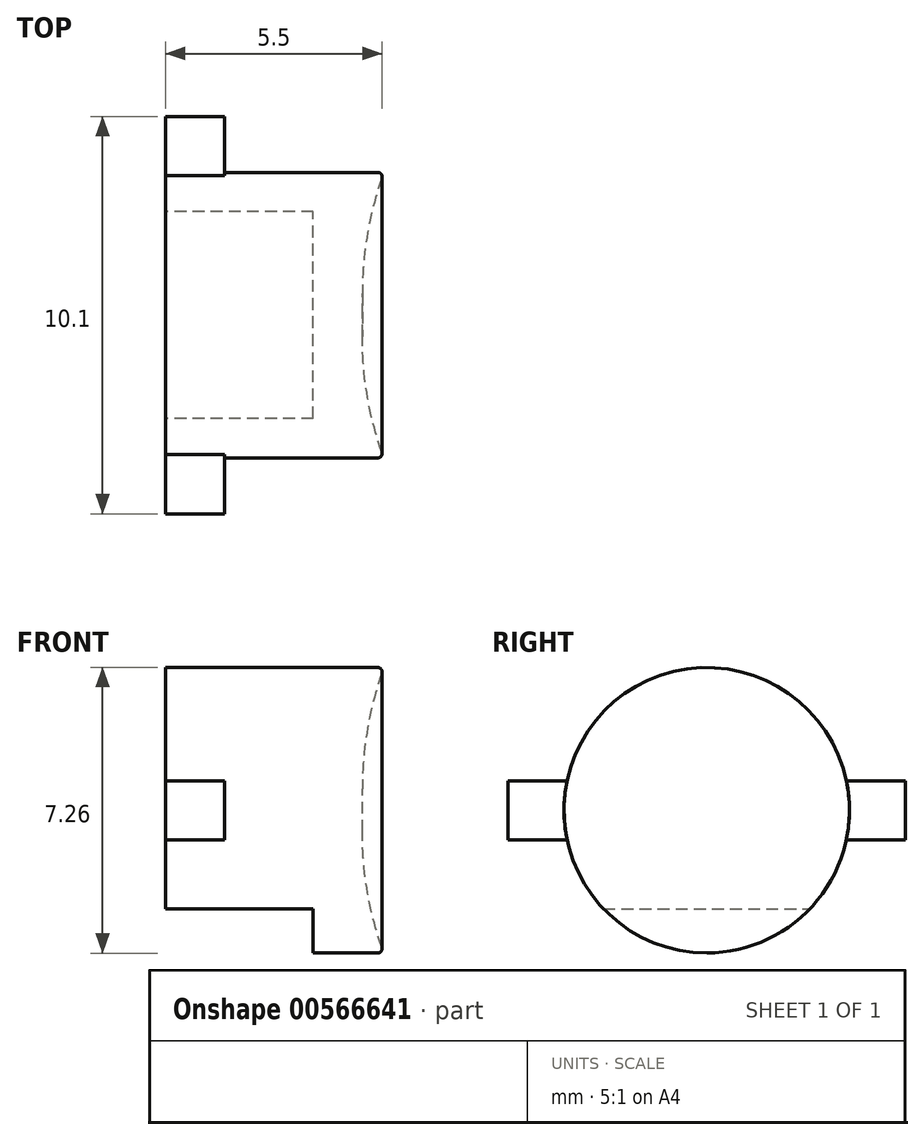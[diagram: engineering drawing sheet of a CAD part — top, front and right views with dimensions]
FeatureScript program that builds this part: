
annotation { "Feature Type Name" : "Feature", "Feature Type Description" : "" }
export const myFeature = defineFeature(function(context is Context, id is Id, definition is map)
    precondition{}
    {
        {
            var Q0;
            Q0=qCreatedBy(makeId("Right.planeOp"),FACE);
            var sketch = newSketch(context, id + "F0", { "sketchPlane" : qUnion([Q0])});
            skCircle(sketch, "E0", {"center": v(0, 0) * mm, "radius": 3.62 * mm});
            skSolve(sketch);
        }
        {
            var Q0;
            Q0=makeQuery(id+"F0.imprint","IMPRINT",FACE,{"disambiguationData":[TD([[makeQuery(id+"F0.imprint","IMPRINT",EDGE,{"derivedFrom":sQuery(id+"F0.wireOp",EDGE,"E0")}),1.0]])]});
            extrude(context, id + "F1", {"entities" : qUnion([Q0]), "endBound" : BoundingType.SYMMETRIC, "depth" : 5.5 * mm, "offsetDistance" : 25 * mm});
        }
        {
            var Q0;
            Q0=makeQuery(id+"F1.opExtrude","CAP_FACE",FACE,{"disambiguationData":[OSD([sQuery(id+"F0.wireOp",EDGE,"E0")])],"isStart":true});
            var sketch = newSketch(context, id + "F2", { "sketchPlane" : qUnion([Q0])});
            skLineSegment(sketch, "E1.left", {"start": v(5.05, -0.75) * mm, "end": v(5.05, 0.75) * mm});
            skLineSegment(sketch, "E2.left", {"start": v(-5.05, 0.75) * mm, "end": v(-5.05, -0.75) * mm});
            skLineSegment(sketch, "E3", {"start": v(5.05, 0.75) * mm, "end": v(3.55, 0.75) * mm});
            skLineSegment(sketch, "E4", {"start": v(5.05, -0.75) * mm, "end": v(3.55, -0.75) * mm});
            skArc(sketch, "E5", {"start": v(-3.55, 0.75) * mm, "mid": v(-3.63, 0) * mm, "end": v(-3.55, -0.75) * mm});
            skLineSegment(sketch, "E6", {"start": v(-5.05, 0.75) * mm, "end": v(-3.55, 0.75) * mm});
            skLineSegment(sketch, "E7", {"start": v(-5.05, -0.75) * mm, "end": v(-3.55, -0.75) * mm});
            skArc(sketch, "E8.trimOffspring", {"start": v(3.55, -0.75) * mm, "mid": v(3.63, 0) * mm, "end": v(3.55, 0.75) * mm});
            skPoint(sketch, "E9", {"position": v(5.05, 0) * mm});
            skPoint(sketch, "E10", {"position": v(-5.05, 0) * mm});
            skSolve(sketch);
        }
        {
            var Q0;
            Q0=qSketchRegion(id+"F2",true);
            extrude(context, id + "F3", {"entities" : qUnion([Q0]), "operationType" : NewBodyOperationType.ADD, "oppositeDirection" : true, "depth" : 1.5 * mm, "offsetDistance" : 25 * mm});
        }
        {
            var Q0;
            Q0=makeQuery(id+"F1.opExtrude","CAP_FACE",FACE,{"disambiguationData":[OSD([sQuery(id+"F0.wireOp",EDGE,"E0")])],"isStart":false});
            var sketch = newSketch(context, id + "F4", { "sketchPlane" : qUnion([Q0])});
            skCircle(sketch, "E11", {"center": v(0, 0) * mm, "radius": 3.5 * mm});
            skSolve(sketch);
        }
        {
            var Q0;
            Q0=qSketchRegion(id+"F4",true);
            extrude(context, id + "F5", {"entities" : qUnion([Q0]), "operationType" : NewBodyOperationType.REMOVE, "oppositeDirection" : true, "depth" : .5 * mm, "offsetDistance" : 25 * mm});
        }
        {
            var Q0;
            Q0=makeQuery(id+"F3.boolean.opBoolean","MERGE",FACE,{"derivedFrom":[makeQuery(id+"F1.opExtrude","CAP_FACE",FACE,{"disambiguationData":[OSD([sQuery(id+"F0.wireOp",EDGE,"E0")])],"isStart":true}),makeQuery(id+"F3.opExtrude","CAP_FACE",FACE,{"disambiguationData":[OSD([sQuery(id+"F2.wireOp",EDGE,"E1.left"),sQuery(id+"F2.wireOp",EDGE,"E3"),sQuery(id+"F2.wireOp",EDGE,"E4"),sQuery(id+"F2.wireOp",EDGE,"E8.trimOffspring")])],"isStart":true}),makeQuery(id+"F3.opExtrude","CAP_FACE",FACE,{"disambiguationData":[OSD([sQuery(id+"F2.wireOp",EDGE,"E2.left"),sQuery(id+"F2.wireOp",EDGE,"E5"),sQuery(id+"F2.wireOp",EDGE,"E6"),sQuery(id+"F2.wireOp",EDGE,"E7")])],"isStart":true})]});
            var sketch = newSketch(context, id + "F6", { "sketchPlane" : qUnion([Q0])});
            skArc(sketch, "E12", {"start": v(-2.62, -2.5) * mm, "mid": v(0, -3.63) * mm, "end": v(2.63, -2.5) * mm});
            skLineSegment(sketch, "E13", {"start": v(2.63, -2.5) * mm, "end": v(-2.62, -2.5) * mm});
            skSolve(sketch);
        }
        {
            var Q0;
            Q0=qSketchRegion(id+"F6",true);
            extrude(context, id + "F7", {"entities" : qUnion([Q0]), "operationType" : NewBodyOperationType.REMOVE, "oppositeDirection" : true, "depth" : 3.75 * mm, "offsetDistance" : 25 * mm});
        }
        {
            var Q0;
            Q0=makeQuery(id+"F5.boolean.opBoolean","COPY",FACE,{"derivedFrom":makeQuery(id+"F5.opExtrude","CAP_FACE",FACE,{"disambiguationData":[OSD([sQuery(id+"F4.wireOp",EDGE,"E11")])],"isStart":false})});
            fillet(context, id + "F8", {"entities" : qUnion([Q0]), "radius" : 9 * mm, "tangentPropagation" : true, "allowEdgeOverflow" : false});
        }
        {
            var Q0;
            Q0=makeQuery(id+"F8.opFillet","BLEND_EDGE",EDGE,{"blendedFrom":[makeQuery(id+"F5.boolean.opBoolean","COPY",EDGE,{"derivedFrom":makeQuery(id+"F5.opExtrude","CAP_EDGE",EDGE,{"disambiguationData":[OSD([sQuery(id+"F4.wireOp",EDGE,"E11")])],"isStart":false})}),makeQuery(id+"F1.opExtrude","CAP_FACE",FACE,{"disambiguationData":[OSD([sQuery(id+"F0.wireOp",EDGE,"E0")])],"isStart":false})],"blendedInto":[makeQuery(id+"F1.opExtrude","CAP_FACE",FACE,{"disambiguationData":[OSD([sQuery(id+"F0.wireOp",EDGE,"E0")])],"isStart":false})]});
            var Q1;
            Q1=makeQuery(id+"F1.opExtrude","CAP_EDGE",EDGE,{"disambiguationData":[OSD([sQuery(id+"F0.wireOp",EDGE,"E0")])],"isStart":false});
            fillet(context, id + "F9", {"entities" : qUnion([Q0, Q1]), "radius" : .1 * mm, "tangentPropagation" : true, "allowEdgeOverflow" : false});
        }
    });
